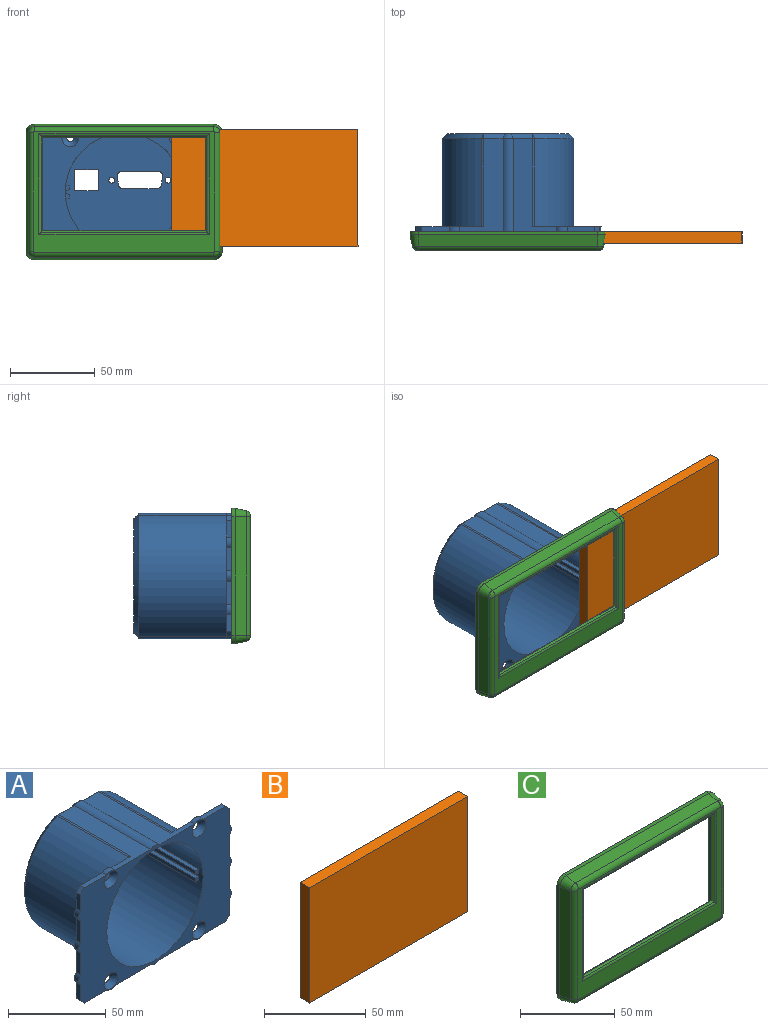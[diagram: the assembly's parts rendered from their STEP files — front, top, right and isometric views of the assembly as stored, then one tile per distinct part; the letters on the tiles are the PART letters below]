
ASSEMBLY  parts=3 mates=2
PART A: 94 faces, bbox 110.5x58.5x74.5 mm
  f0: cylinder r=34.75mm len=69.5mm, axis (0,-1,0), area 11487.5mm2, adj f1,f32,f60,f61,f63,f64,f65,f67
  f1: plane 69.5x69.5mm, normal (0,-1,0), area 3319.3mm2, adj f0,f60,f61,f62,f64,f65,f66,f68
  f2: plane 74x40.61mm, normal (0,1,0), area 1545.8mm2, adj f7,f8,f9,f10,f11,f12,f13,f14
  f3: plane 74x40.61mm, normal (0,1,0), area 1545.8mm2, adj f4,f5,f21,f22,f23,f24,f25,f26
  f4: cylinder r=5mm len=6mm, axis (0,1,0), area 19.3mm2, adj f3,f5,f31,f32
  f5: plane 55x25.82mm, normal (0,0,-1), area 669.6mm2, adj f3,f4,f6,f32,f51,f52
  f6: cylinder r=5mm len=55mm, axis (0,1,0), area 353.9mm2, adj f5,f7,f32,f49
  f7: plane 55x25.82mm, normal (0,0,-1), area 669.6mm2, adj f2,f6,f8,f32,f44,f46
  f8: cylinder r=5mm len=6mm, axis (0,1,0), area 19.3mm2, adj f2,f7,f9,f32
  f9: plane 16.18x3mm, normal (0,0,-1), area 48.5mm2, adj f2,f8,f32,f33
  f10: plane 10x3mm, normal (1,0,0), area 30mm2, adj f2,f11,f32,f33
  f11: cylinder r=5mm len=6mm, axis (0,1,0), area 19.3mm2, adj f2,f10,f12,f32
  f12: plane 14x3mm, normal (1,0,0), area 42mm2, adj f2,f11,f13,f32
  f13: cylinder r=5mm len=6mm, axis (0,1,0), area 19.3mm2, adj f2,f12,f14,f32
  f14: plane 14x3mm, normal (1,0,0), area 42mm2, adj f2,f13,f15,f32
  f15: cylinder r=5mm len=6mm, axis (0,1,0), area 19.3mm2, adj f2,f14,f16,f32
  f16: plane 10x3mm, normal (1,0,0), area 30mm2, adj f2,f15,f32,f36
  f17: plane 16.18x3mm, normal (0,0,1), area 48.5mm2, adj f2,f18,f32,f36
  f18: cylinder r=5mm len=6mm, axis (0,1,0), area 19.3mm2, adj f2,f17,f19,f32
  f19: plane 55x25.82mm, normal (0,0,1), area 669.6mm2, adj f2,f18,f20,f32,f48,f53
  f20: cylinder r=5mm len=55mm, axis (0,1,0), area 353.9mm2, adj f19,f21,f32,f55
  f21: plane 55x25.82mm, normal (0,0,1), area 669.6mm2, adj f3,f20,f22,f32,f57,f59
  f22: cylinder r=5mm len=6mm, axis (0,1,0), area 19.3mm2, adj f3,f21,f23,f32
  f23: plane 16.18x3mm, normal (0,0,1), area 48.5mm2, adj f3,f22,f32,f35
  f24: plane 10x3mm, normal (-1,0,0), area 30mm2, adj f3,f25,f32,f35
  f25: cylinder r=5mm len=6mm, axis (0,1,0), area 19.3mm2, adj f3,f24,f26,f32
  f26: plane 14x3mm, normal (-1,0,0), area 42mm2, adj f3,f25,f27,f32
  f27: cylinder r=5mm len=6mm, axis (0,1,0), area 19.3mm2, adj f3,f26,f28,f32
  f28: plane 14x3mm, normal (-1,0,0), area 42mm2, adj f3,f27,f29,f32
  f29: cylinder r=5mm len=6mm, axis (0,1,0), area 19.3mm2, adj f3,f28,f30,f32
  f30: plane 10x3mm, normal (-1,0,0), area 30mm2, adj f3,f29,f32,f34
  f31: plane 16.18x3mm, normal (0,0,-1), area 48.5mm2, adj f3,f4,f32,f34
  f32: plane 110x74mm, normal (0,-1,0), area 3699.2mm2, adj f0,f4,f5,f6,f7,f8,f9,f10
  f33: plane 3x3mm, normal (0.71,0,-0.71), area 12.7mm2, adj f2,f9,f10,f32
  f34: plane 3x3mm, normal (-0.71,0,-0.71), area 12.7mm2, adj f3,f30,f31,f32
  f35: plane 3x3mm, normal (-0.71,0,0.71), area 12.7mm2, adj f3,f23,f24,f32
  f36: plane 3x3mm, normal (0.71,0,0.71), area 12.7mm2, adj f2,f16,f17,f32
  f37: cone r=2mm half-angle=45deg, axis (0,-1,0), area 93.3mm2, adj f2,f32
  f38: cone r=2mm half-angle=45deg, axis (0,-1,0), area 93.3mm2, adj f2,f32
  f39: cone r=2mm half-angle=45deg, axis (0,-1,0), area 93.3mm2, adj f3,f32
  f40: cone r=2mm half-angle=45deg, axis (0,-1,0), area 93.3mm2, adj f3,f32
  f41: cylinder r=39mm len=71.5mm, axis (0,-1,0), area 4703.6mm2, adj f2,f44,f47,f48
  f42: cylinder r=39mm len=71.5mm, axis (0,-1,0), area 4703.6mm2, adj f3,f51,f56,f59
  f43: plane 72x68mm, normal (0,1,0), area 3509.5mm2, adj f46,f47,f49,f52,f53,f55,f56,f57
  f44: plane 52x1.2mm, normal (0.2,0,-0.98), area 63.7mm2, adj f2,f7,f41,f45
  f45: plane 3x3mm, normal (0.15,0.7,-0.7), area 2.6mm2, adj f44,f46,f47
  f46: plane 13.13x3.48mm, normal (0,0.71,-0.71), area 50.8mm2, adj f7,f43,f45,f49
  f47: cone r=36mm half-angle=45deg, axis (0,-1,0), area 369mm2, adj f41,f43,f45,f50
  f48: plane 52x1.2mm, normal (0.2,0,0.98), area 63.7mm2, adj f2,f19,f41,f50
  f49: cone r=2mm half-angle=45deg, axis (0,-1,0), area 24.2mm2, adj f6,f43,f46,f52
  f50: plane 3x3mm, normal (0.15,0.7,0.7), area 2.6mm2, adj f47,f48,f53
  f51: plane 52x1.2mm, normal (-0.2,0,-0.98), area 63.7mm2, adj f3,f5,f42,f54
  f52: plane 13.13x3.48mm, normal (0,0.71,-0.71), area 50.8mm2, adj f5,f43,f49,f54
  f53: plane 13.13x3.48mm, normal (0,0.71,0.71), area 50.8mm2, adj f19,f43,f50,f55
  f54: plane 3x3mm, normal (-0.15,0.7,-0.7), area 2.6mm2, adj f51,f52,f56
  f55: cone r=5mm half-angle=45deg, axis (0,-1,0), area 24.2mm2, adj f20,f43,f53,f57
  f56: cone r=36mm half-angle=45deg, axis (0,-1,0), area 369mm2, adj f42,f43,f54,f58
  f57: plane 13.13x3.48mm, normal (0,0.71,0.71), area 50.8mm2, adj f21,f43,f55,f58
  f58: plane 3x3mm, normal (-0.15,0.7,0.7), area 2.6mm2, adj f56,f57,f59
  f59: plane 52x1.2mm, normal (-0.2,0,0.98), area 63.7mm2, adj f3,f21,f42,f58
  f60: plane 52x2.33mm, normal (0,0,1), area 121.4mm2, adj f0,f1,f62,f63
  f61: plane 52x0.5mm, normal (0,0,-1), area 26mm2, adj f0,f1,f63,f77
  f62: plane 52x2.3mm, normal (1,0,0), area 119.6mm2, adj f1,f60,f63,f77
  f63: plane 2.5x2.5mm, normal (0,-1,0), area 5.9mm2, adj f0,f60,f61,f62,f77
  f64: plane 52x0.5mm, normal (0,0,1), area 26mm2, adj f0,f1,f67,f78
  f65: plane 52x2.33mm, normal (0,0,-1), area 121.4mm2, adj f0,f1,f66,f67
  f66: plane 52x2.3mm, normal (1,0,0), area 119.6mm2, adj f1,f65,f67,f78
  f67: plane 2.5x2.5mm, normal (0,-1,0), area 5.9mm2, adj f0,f64,f65,f66,f78
  f68: plane 52x2.33mm, normal (0,0,1), area 121.4mm2, adj f0,f1,f69,f71
  f69: plane 52x2.3mm, normal (-1,0,0), area 119.6mm2, adj f1,f68,f71,f79
  f70: plane 52x0.5mm, normal (0,0,-1), area 26mm2, adj f0,f1,f71,f79
  f71: plane 2.5x2.5mm, normal (0,-1,0), area 5.9mm2, adj f0,f68,f69,f70,f79
  f72: plane 52x0.5mm, normal (0,0,1), area 26mm2, adj f0,f1,f75,f76
  f73: plane 52x2.3mm, normal (-1,0,0), area 119.6mm2, adj f1,f74,f75,f76
  f74: plane 52x2.33mm, normal (0,0,-1), area 121.4mm2, adj f0,f1,f73,f75
  f75: plane 2.5x2.5mm, normal (0,-1,0), area 5.9mm2, adj f0,f72,f73,f74,f76
  f76: plane 52x2mm, normal (-0.1,0,1), area 104.5mm2, adj f1,f72,f73,f75
  f77: plane 52x2mm, normal (0.1,0,-1), area 104.5mm2, adj f1,f61,f62,f63
  f78: plane 52x2mm, normal (0.1,0,1), area 104.5mm2, adj f1,f64,f66,f67
  f79: plane 52x2mm, normal (-0.1,0,-1), area 104.5mm2, adj f1,f69,f70,f71
  f80: cylinder r=1.75mm len=3.5mm, axis (0,-1,0), area 33mm2, adj f1,f43
  f81: cylinder r=1.75mm len=3.5mm, axis (0,-1,0), area 33mm2, adj f1,f43
  f82: plane 20.28x3mm, normal (0,0,1), area 60.8mm2, adj f1,f43,f91,f92
  f83: plane 5x3mm, normal (-0.98,0,0.17), area 15.2mm2, adj f1,f43,f90,f91
  f84: plane 22.04x3mm, normal (0,0,-1), area 66.1mm2, adj f1,f43,f90,f93
  f85: plane 5x3mm, normal (0.98,0,0.17), area 15.2mm2, adj f1,f43,f92,f93
  f86: plane 12.5x3mm, normal (1,0,0), area 37.5mm2, adj f1,f43,f87,f89
  f87: plane 14x3mm, normal (0,0,1), area 42mm2, adj f1,f43,f86,f88
  f88: plane 12.5x3mm, normal (-1,0,0), area 37.5mm2, adj f1,f43,f87,f89
  f89: plane 14x3mm, normal (0,0,-1), area 42mm2, adj f1,f43,f86,f88
  f90: cylinder r=2.5mm len=3mm, axis (0,1,0), area 13.1mm2, adj f1,f43,f83,f84
  f91: cylinder r=2.5mm len=3mm, axis (0,-1,0), area 10.5mm2, adj f1,f43,f82,f83
  f92: cylinder r=2.5mm len=3mm, axis (0,1,0), area 10.5mm2, adj f1,f43,f82,f85
  f93: cylinder r=2.5mm len=3mm, axis (0,-1,0), area 13.1mm2, adj f1,f43,f84,f85
PART B: 6 faces, bbox 110x6.7x69.3 mm
  f0: plane 110x6.7mm, normal (0,0,1), area 737mm2, adj f1,f3,f4,f5
  f1: plane 69.3x6.7mm, normal (-1,0,0), area 464.3mm2, adj f0,f2,f4,f5
  f2: plane 110x6.7mm, normal (0,0,-1), area 737mm2, adj f1,f3,f4,f5
  f3: plane 69.3x6.7mm, normal (1,0,0), area 464.3mm2, adj f0,f2,f4,f5
  f4: plane 110x69.3mm, normal (0,-1,0), area 7623mm2, adj f0,f1,f2,f3
  f5: plane 110x69.3mm, normal (0,1,0), area 7623mm2, adj f0,f1,f2,f3
PART C: 43 faces, bbox 116x11x80 mm
  f0: plane 106x2mm, normal (0,0,1), area 212mm2, adj f4,f15,f18,f22
  f1: plane 70x2mm, normal (-1,0,0), area 140mm2, adj f4,f15,f16,f19
  f2: plane 106x2mm, normal (0,0,-1), area 212mm2, adj f4,f16,f17,f23
  f3: plane 70x2mm, normal (1,0,0), area 140mm2, adj f4,f17,f18,f26
  f4: plane 116x80mm, normal (0,1,0), area 1118.5mm2, adj f0,f1,f2,f3,f6,f7,f8,f9
  f5: plane 107.19x71.19mm, normal (0,-1,0), area 1625.1mm2, adj f27,f28,f29,f30,f31,f32,f33,f34
  f6: plane 74x9mm, normal (-1,0,0), area 666mm2, adj f4,f7,f9,f10
  f7: plane 110x9mm, normal (0,0,1), area 990mm2, adj f4,f6,f8,f10
  f8: plane 74x9mm, normal (1,0,0), area 666mm2, adj f4,f7,f9,f10
  f9: plane 110x9mm, normal (0,0,-1), area 990mm2, adj f4,f6,f8,f10
  f10: plane 110x74mm, normal (0,1,0), area 2860mm2, adj f6,f7,f8,f9,f11,f12,f13,f14
  f11: plane 55x0.5mm, normal (1,0,0), area 27.5mm2, adj f10,f12,f14,f35
  f12: plane 96x0.5mm, normal (0,0,1), area 48mm2, adj f10,f11,f13,f37
  f13: plane 55x0.5mm, normal (-1,0,0), area 27.5mm2, adj f10,f12,f14,f38
  f14: plane 96x0.5mm, normal (0,0,-1), area 48mm2, adj f10,f11,f13,f36
  f15: cylinder r=5mm len=5mm, axis (0,1,0), area 15.7mm2, adj f0,f1,f4,f20
  f16: cylinder r=5mm len=5mm, axis (0,-1,0), area 15.7mm2, adj f1,f2,f4,f21
  f17: cylinder r=5mm len=5mm, axis (0,1,0), area 15.7mm2, adj f2,f3,f4,f25
  f18: cylinder r=5mm len=5mm, axis (0,-1,0), area 15.7mm2, adj f0,f3,f4,f24
  f19: plane 70x6.65mm, normal (-0.98,-0.22,0), area 476.9mm2, adj f1,f20,f21,f30
  f20: cone r=3mm half-angle=12.5deg, axis (0,1,0), area 45.6mm2, adj f15,f19,f22,f28
  f21: cone r=3mm half-angle=12.5deg, axis (0,1,0), area 45.6mm2, adj f16,f19,f23,f32
  f22: plane 106x6.65mm, normal (0,-0.22,0.98), area 722.2mm2, adj f0,f20,f24,f27
  f23: plane 106x6.65mm, normal (0,-0.22,-0.98), area 722.2mm2, adj f2,f21,f25,f34
  f24: cone r=3mm half-angle=12.5deg, axis (0,1,0), area 45.6mm2, adj f18,f22,f26,f29
  f25: cone r=3mm half-angle=12.5deg, axis (0,1,0), area 45.6mm2, adj f17,f23,f26,f33
  f26: plane 70x6.65mm, normal (0.98,-0.22,0), area 476.9mm2, adj f3,f24,f25,f31
  f27: cylinder r=3mm len=106mm, axis (-1,0,0), area 430mm2, adj f5,f22,f28,f29
  f28: torus R=0.59mm, axis (0,-1,0), area 14.9mm2, adj f5,f20,f27,f30
  f29: torus R=0.59mm, axis (0,-1,0), area 14.9mm2, adj f5,f24,f27,f31
  f30: cylinder r=3mm len=70mm, axis (0,0,1), area 283.9mm2, adj f5,f19,f28,f32
  f31: cylinder r=3mm len=70mm, axis (0,0,1), area 283.9mm2, adj f5,f26,f29,f33
  f32: torus R=0.59mm, axis (0,-1,0), area 14.9mm2, adj f5,f21,f30,f34
  f33: torus R=0.59mm, axis (0,-1,0), area 14.9mm2, adj f5,f25,f31,f34
  f34: cylinder r=3mm len=106mm, axis (-1,0,0), area 430mm2, adj f5,f23,f32,f33
  f35: plane 56.83x0.91mm, normal (0.71,-0.71,0), area 72.3mm2, adj f11,f36,f37,f39
  f36: plane 97.83x0.91mm, normal (0,-0.71,-0.71), area 125.3mm2, adj f14,f35,f38,f40
  f37: plane 97.83x0.91mm, normal (0,-0.71,0.71), area 125.3mm2, adj f12,f35,f38,f41
  f38: plane 56.83x0.91mm, normal (-0.71,-0.71,0), area 72.3mm2, adj f13,f36,f37,f42
  f39: cylinder r=2mm len=59.66mm, axis (0,0,1), area 91.4mm2, adj f5,f35,f40,f41
  f40: cylinder r=2mm len=100.66mm, axis (-1,0,0), area 155.8mm2, adj f5,f36,f39,f42
  f41: cylinder r=2mm len=100.66mm, axis (-1,0,0), area 155.8mm2, adj f5,f37,f39,f42
  f42: cylinder r=2mm len=59.66mm, axis (0,0,1), area 91.4mm2, adj f5,f38,f40,f41
PLACE A t=(-40.43,30.43,-15.84)mm
PLACE B t=(99.3,27.43,-12.14)mm
PLACE C t=(-44.44,16.53,-19.84)mm
MATE planar B.f5 <-> A.f0  axis (0,1,0) through (96.85,27.43,22.51)mm
MATE planar C.f9 <-> B.f0  axis (0,0,-1) through (13.56,18.53,57.16)mm
